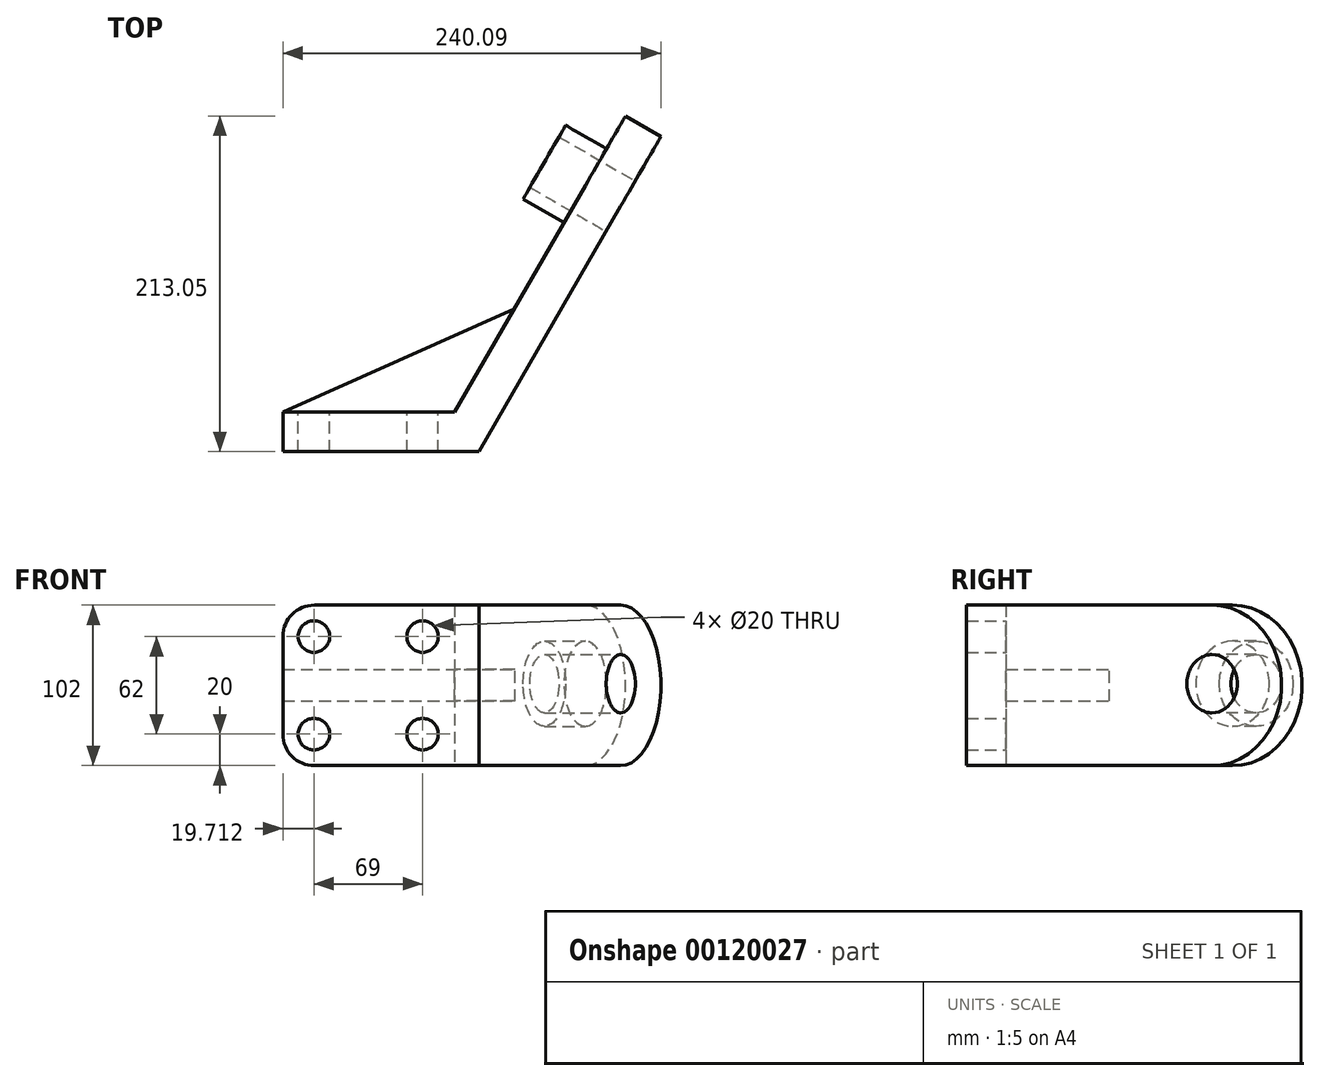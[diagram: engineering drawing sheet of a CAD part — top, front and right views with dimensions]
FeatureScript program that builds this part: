
annotation { "Feature Type Name" : "Feature", "Feature Type Description" : "" }
export const myFeature = defineFeature(function(context is Context, id is Id, definition is map)
    precondition{}
    {
        {
            var Q0;
            Q0=qCreatedBy(makeId("Top.planeOp"),FACE);
            var sketch = newSketch(context, id + "F0", { "sketchPlane" : qUnion([Q0])});
            skLineSegment(sketch, "E0", {"start": v(-151.63, -156.8) * mm, "end": v(-27.04, -156.8) * mm});
            skLineSegment(sketch, "E1", {"start": v(-27.04, -156.8) * mm, "end": v(88.46, 43.26) * mm});
            skLineSegment(sketch, "E2", {"start": v(88.46, 43.26) * mm, "end": v(65.95, 56.26) * mm});
            skLineSegment(sketch, "E3", {"start": v(65.95, 56.26) * mm, "end": v(-42.63, -131.8) * mm});
            skLineSegment(sketch, "E4", {"start": v(-42.63, -131.8) * mm, "end": v(-151.63, -131.8) * mm});
            skLineSegment(sketch, "E5", {"start": v(-151.63, -131.8) * mm, "end": v(-151.63, -156.8) * mm});
            skSolve(sketch);
        }
        {
            var Q0;
            Q0 = qSketchRegion(id + "F0", true);
            extrude(context, id + "F1", {"entities" : qUnion([Q0]), "depth" : 102 * mm});
        }
        {
            var Q0;
            Q0=makeQuery(id+"F1.opExtrude","SWEPT_FACE",FACE,{"disambiguationData":[OSD([sQuery(id+"F0.wireOp",EDGE,"E3")])]});
            var sketch = newSketch(context, id + "F2", { "sketchPlane" : qUnion([Q0])});
            skCircle(sketch, "E6", {"center": v(-30.7, 52.06) * mm, "radius": 18.5 * mm});
            skCircle(sketch, "E7", {"center": v(-30.7, 52.06) * mm, "radius": 27 * mm});
            skLineSegment(sketch, "E8", {"start": v(-30.7, 0) * mm, "end": v(-30.7, 102) * mm, "construction": true});
            skSolve(sketch);
        }
        {
            var Q0;
            Q0=makeQuery(id+"F2.imprint","IMPRINT",FACE,{"disambiguationData":[TD([[makeQuery(id+"F2.imprint","IMPRINT",EDGE,{"derivedFrom":sQuery(id+"F2.wireOp",EDGE,"E6")}),-1.0]])]});
            extrude(context, id + "F3", {"entities" : qUnion([Q0]), "operationType" : NewBodyOperationType.ADD, "depth" : 30 * mm});
        }
        {
            var Q0;
            Q0=makeQuery(id+"F1.opExtrude","SWEPT_FACE",FACE,{"disambiguationData":[OSD([sQuery(id+"F0.wireOp",EDGE,"E4")])]});
            var sketch = newSketch(context, id + "F4", { "sketchPlane" : qUnion([Q0])});
            skCircle(sketch, "E9", {"center": v(62.92, 20) * mm, "radius": 10 * mm});
            skCircle(sketch, "E10.0.1.0", {"center": v(62.92, 82) * mm, "radius": 10 * mm});
            skCircle(sketch, "E10.1.0.0", {"center": v(131.92, 20) * mm, "radius": 10 * mm});
            skCircle(sketch, "E10.1.1.0", {"center": v(131.92, 82) * mm, "radius": 10 * mm});
            skLineSegment(sketch, "E10.direction1", {"start": v(62.92, 20) * mm, "end": v(131.92, 20) * mm, "construction": true});
            skLineSegment(sketch, "E10.direction2", {"start": v(62.92, 20) * mm, "end": v(62.92, 82) * mm, "construction": true});
            skSolve(sketch);
        }
        {
            var Q0;
            Q0=makeQuery(id+"F4.imprint","IMPRINT",FACE,{"disambiguationData":[TD([[makeQuery(id+"F4.imprint","IMPRINT",EDGE,{"derivedFrom":sQuery(id+"F4.wireOp",EDGE,"E10.0.1.0")}),1.0]])]});
            var Q1;
            Q1=makeQuery(id+"F4.imprint","IMPRINT",FACE,{"disambiguationData":[TD([[makeQuery(id+"F4.imprint","IMPRINT",EDGE,{"derivedFrom":sQuery(id+"F4.wireOp",EDGE,"E10.1.1.0")}),1.0]])]});
            var Q2;
            Q2=makeQuery(id+"F4.imprint","IMPRINT",FACE,{"disambiguationData":[TD([[makeQuery(id+"F4.imprint","IMPRINT",EDGE,{"derivedFrom":sQuery(id+"F4.wireOp",EDGE,"E10.1.0.0")}),1.0]])]});
            var Q3;
            Q3=makeQuery(id+"F4.imprint","IMPRINT",FACE,{"disambiguationData":[TD([[makeQuery(id+"F4.imprint","IMPRINT",EDGE,{"derivedFrom":sQuery(id+"F4.wireOp",EDGE,"E9")}),1.0]])]});
            extrude(context, id + "F5", {"entities" : qUnion([Q0, Q1, Q2, Q3]), "operationType" : NewBodyOperationType.REMOVE, "oppositeDirection" : true, "depth" : 50 * mm});
        }
        {
            var Q0;
            Q0=makeQuery(id+"F1.opExtrude","CAP_EDGE",EDGE,{"disambiguationData":[OSD([sQuery(id+"F0.wireOp",EDGE,"E2")])],"isStart":false});
            var Q1;
            Q1=makeQuery(id+"F1.opExtrude","CAP_EDGE",EDGE,{"disambiguationData":[OSD([sQuery(id+"F0.wireOp",EDGE,"E2")])],"isStart":true});
            fillet(context, id + "F6", {"entities" : qUnion([Q0, Q1]), "radius" : 51 * mm, "tangentPropagation" : true, "allowEdgeOverflow" : false});
        }
        {
            var Q0;
            Q0=makeQuery(id+"F1.opExtrude","CAP_FACE",FACE,{"disambiguationData":[OSD([sQuery(id+"F0.wireOp",EDGE,"E0"),sQuery(id+"F0.wireOp",EDGE,"E1"),sQuery(id+"F0.wireOp",EDGE,"E2"),sQuery(id+"F0.wireOp",EDGE,"E3"),sQuery(id+"F0.wireOp",EDGE,"E4"),sQuery(id+"F0.wireOp",EDGE,"E5")])],"isStart":true});
            cPlane(context, id + "F7", {"entities" : qUnion([Q0]), "cplaneType" : CPlaneType.OFFSET, "offset" : 51 * mm, "oppositeDirection" : true, "width" : 150 * mm, "height" : 150 * mm});
        }
        {
            var Q0;
            Q0=qCreatedBy(id+"F7.planeOp",FACE);
            var sketch = newSketch(context, id + "F8", { "sketchPlane" : qUnion([Q0])});
            skLineSegment(sketch, "E11", {"start": v(-151.63, 131.8) * mm, "end": v(-4.31, 66.15) * mm});
            skLineSegment(sketch, "E12", {"start": v(-4.31, 66.15) * mm, "end": v(-42.63, 131.8) * mm});
            skLineSegment(sketch, "E13", {"start": v(-151.63, 131.8) * mm, "end": v(-42.63, 131.8) * mm});
            skSolve(sketch);
        }
        {
            var Q0;
            Q0 = qSketchRegion(id + "F8", true);
            extrude(context, id + "F9", {"entities" : qUnion([Q0]), "endBound" : BoundingType.SYMMETRIC, "depth" : 20 * mm});
        }
        {
            var Q0;
            Q0=makeQuery(id+"F2.imprint","IMPRINT",FACE,{"disambiguationData":[TD([[makeQuery(id+"F2.imprint","IMPRINT",EDGE,{"derivedFrom":sQuery(id+"F2.wireOp",EDGE,"E7")}),-1.0]])]});
            var sketch = newSketch(context, id + "F10", { "sketchPlane" : qUnion([Q0])});
            skCircle(sketch, "E14.0", {"center": v(-30.7, 52.06) * mm, "radius": 18.5 * mm});
            skSolve(sketch);
        }
        {
            var Q0;
            Q0 = qSketchRegion(id + "F10", true);
            extrude(context, id + "F11", {"entities" : qUnion([Q0]), "operationType" : NewBodyOperationType.REMOVE, "oppositeDirection" : true, "depth" : 30 * mm});
        }
        {
            var Q0;
            Q0=makeQuery(id+"F1.opExtrude","CAP_EDGE",EDGE,{"disambiguationData":[OSD([sQuery(id+"F0.wireOp",EDGE,"E5")])],"isStart":false});
            var Q1;
            Q1=makeQuery(id+"F1.opExtrude","CAP_EDGE",EDGE,{"disambiguationData":[OSD([sQuery(id+"F0.wireOp",EDGE,"E5")])],"isStart":true});
            fillet(context, id + "F12", {"entities" : qUnion([Q0, Q1]), "radius" : 20 * mm, "tangentPropagation" : true, "allowEdgeOverflow" : false});
        }
    });
